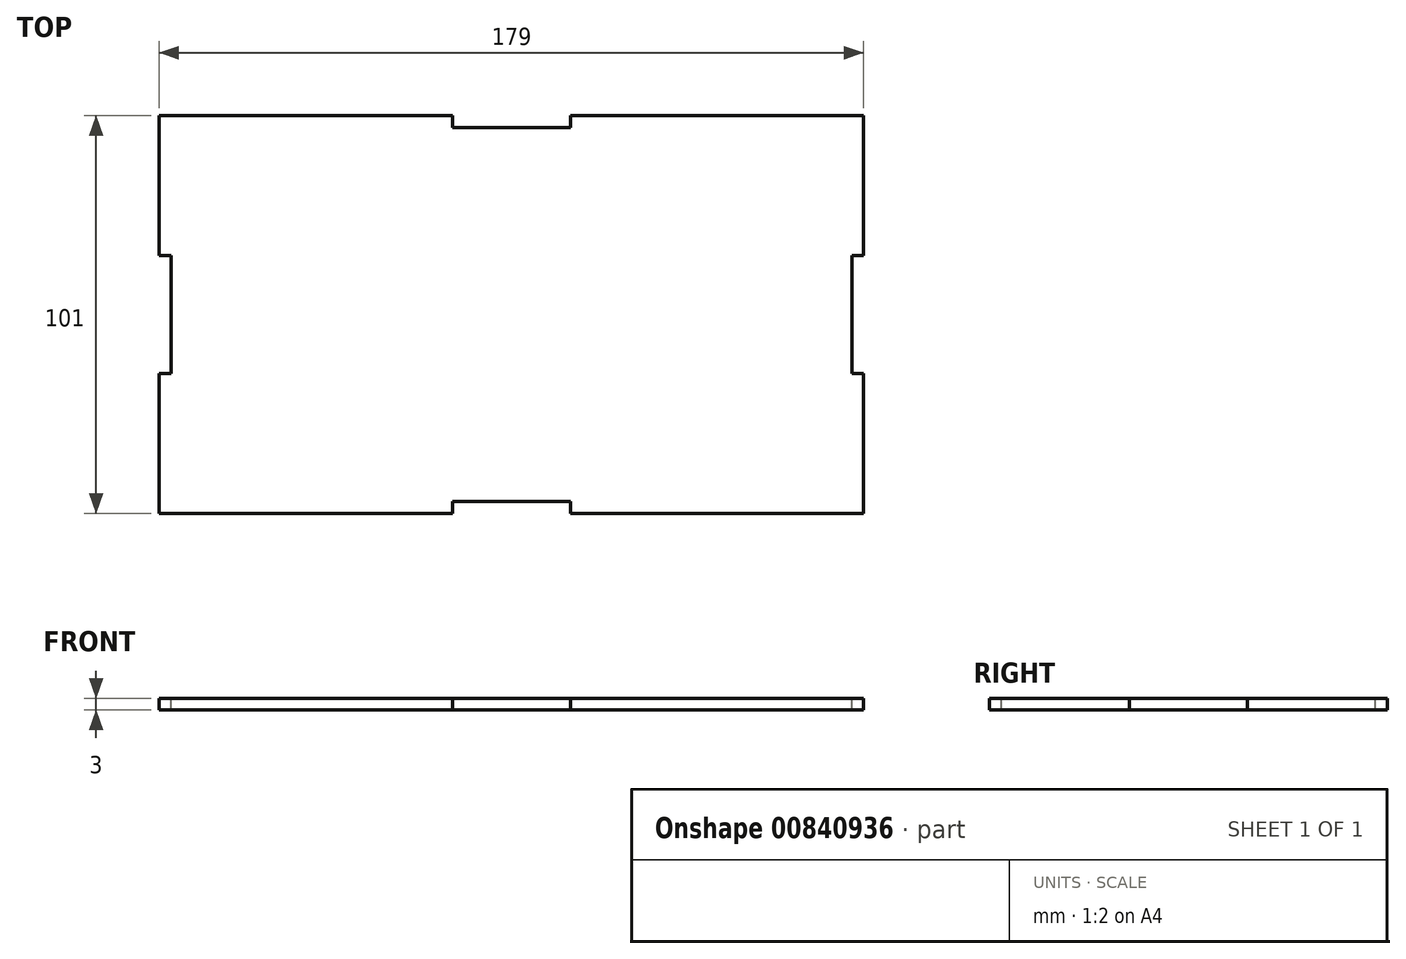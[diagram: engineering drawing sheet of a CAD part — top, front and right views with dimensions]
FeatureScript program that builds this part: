
annotation { "Feature Type Name" : "Feature", "Feature Type Description" : "" }
export const myFeature = defineFeature(function(context is Context, id is Id, definition is map)
    precondition{}
    {
        {
            var Q0;
            Q0=qCreatedBy(makeId("Top.planeOp"),FACE);
            var sketch = newSketch(context, id + "F0", { "sketchPlane" : qUnion([Q0])});
            skLineSegment(sketch, "E0.bottom", {"start": v(-57.94, 74.97) * mm, "end": v(121.06, 74.97) * mm});
            skLineSegment(sketch, "E0.top", {"start": v(-57.94, -26.03) * mm, "end": v(121.06, -26.03) * mm});
            skLineSegment(sketch, "E0.left", {"start": v(-57.94, 74.97) * mm, "end": v(-57.94, -26.03) * mm});
            skLineSegment(sketch, "E0.right", {"start": v(121.06, 74.97) * mm, "end": v(121.06, -26.03) * mm});
            skSolve(sketch);
        }
        {
            var Q0;
            Q0 = qSketchRegion(id + "F0", true);
            extrude(context, id + "F1", {"entities" : qUnion([Q0]), "depth" : 3 * mm, "offsetDistance" : 25 * mm});
        }
        {
            var Q0;
            Q0=makeQuery(id+"F1.opExtrude","CAP_FACE",FACE,{"disambiguationData":[OSD([sQuery(id+"F0.wireOp",EDGE,"E0.bottom"),sQuery(id+"F0.wireOp",EDGE,"E0.top"),sQuery(id+"F0.wireOp",EDGE,"E0.left"),sQuery(id+"F0.wireOp",EDGE,"E0.right")])],"isStart":false});
            var sketch = newSketch(context, id + "F2", { "sketchPlane" : qUnion([Q0])});
            skLineSegment(sketch, "E1", {"start": v(-57.94, 24.47) * mm, "end": v(121.06, 24.47) * mm, "construction": true});
            skLineSegment(sketch, "E2", {"start": v(31.56, 74.97) * mm, "end": v(31.56, -26.03) * mm, "construction": true});
            skLineSegment(sketch, "E3.bottom", {"start": v(16.56, 74.97) * mm, "end": v(46.56, 74.97) * mm});
            skLineSegment(sketch, "E3.top", {"start": v(16.56, 71.97) * mm, "end": v(46.56, 71.97) * mm});
            skLineSegment(sketch, "E3.left", {"start": v(16.56, 74.97) * mm, "end": v(16.56, 71.97) * mm});
            skLineSegment(sketch, "E3.right", {"start": v(46.56, 74.97) * mm, "end": v(46.56, 71.97) * mm});
            skLineSegment(sketch, "E4.bottom", {"start": v(-57.94, 39.47) * mm, "end": v(-54.94, 39.47) * mm});
            skLineSegment(sketch, "E4.top", {"start": v(-57.94, 9.47) * mm, "end": v(-54.94, 9.47) * mm});
            skLineSegment(sketch, "E4.left", {"start": v(-57.94, 39.47) * mm, "end": v(-57.94, 9.47) * mm});
            skLineSegment(sketch, "E4.right", {"start": v(-54.94, 39.47) * mm, "end": v(-54.94, 9.47) * mm});
            skLineSegment(sketch, "E5.MirrorCS", {"start": v(121.06, 9.47) * mm, "end": v(118.06, 9.47) * mm});
            skLineSegment(sketch, "E6.MirrorCS", {"start": v(121.06, 39.47) * mm, "end": v(118.06, 39.47) * mm});
            skLineSegment(sketch, "E7.MirrorCS", {"start": v(118.06, 39.47) * mm, "end": v(118.06, 9.47) * mm});
            skLineSegment(sketch, "E8.MirrorCS", {"start": v(121.06, 39.47) * mm, "end": v(121.06, 9.47) * mm});
            skLineSegment(sketch, "E9.MirrorCS", {"start": v(46.56, -26.03) * mm, "end": v(46.56, -23.03) * mm});
            skLineSegment(sketch, "E10.MirrorCS", {"start": v(16.56, -26.03) * mm, "end": v(16.56, -23.03) * mm});
            skLineSegment(sketch, "E11.MirrorCS", {"start": v(16.56, -23.03) * mm, "end": v(46.56, -23.03) * mm});
            skLineSegment(sketch, "E12.MirrorCS", {"start": v(16.56, -26.03) * mm, "end": v(46.56, -26.03) * mm});
            skSolve(sketch);
        }
        {
            var Q0;
            Q0 = qSketchRegion(id + "F2", true);
            extrude(context, id + "F3", {"entities" : qUnion([Q0]), "operationType" : NewBodyOperationType.REMOVE, "oppositeDirection" : true, "depth" : 25 * mm, "offsetDistance" : 25 * mm});
        }
    });
